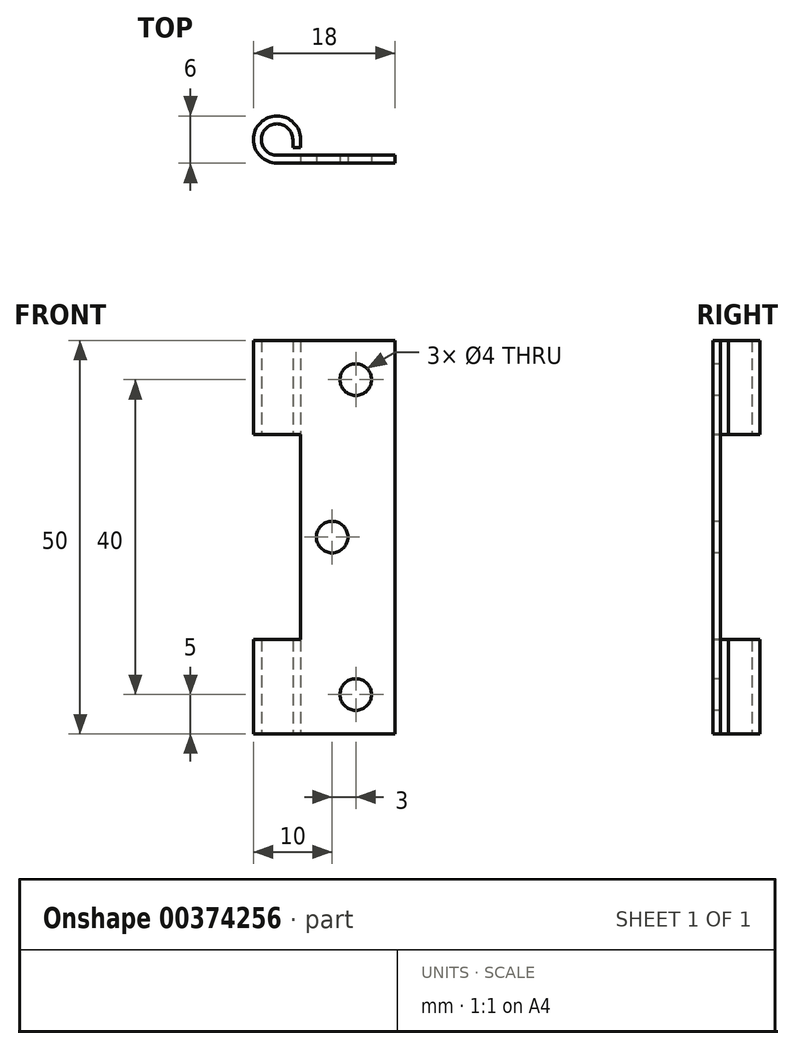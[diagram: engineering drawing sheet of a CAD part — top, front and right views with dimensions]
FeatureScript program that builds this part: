
annotation { "Feature Type Name" : "Feature", "Feature Type Description" : "" }
export const myFeature = defineFeature(function(context is Context, id is Id, definition is map)
    precondition{}
    {
        {
            var Q0;
            Q0=qCreatedBy(makeId("Top.planeOp"),FACE);
            var sketch = newSketch(context, id + "F0", { "sketchPlane" : qUnion([Q0])});
            skLineSegment(sketch, "E0", {"start": v(15, 0) * mm, "end": v(0, 0) * mm});
            skArc(sketch, "E1", {"start": v(3, 3) * mm, "mid": v(-2.12, 5.12) * mm, "end": v(0, 0) * mm});
            skArc(sketch, "E2", {"start": v(2, 3) * mm, "mid": v(-1.41, 4.41) * mm, "end": v(0, 1) * mm});
            skLineSegment(sketch, "E3", {"start": v(0, 1) * mm, "end": v(15, 1) * mm});
            skLineSegment(sketch, "E4", {"start": v(15, 1) * mm, "end": v(15, 0) * mm});
            skLineSegment(sketch, "E5", {"start": v(2, 3) * mm, "end": v(2, 2) * mm});
            skLineSegment(sketch, "E6", {"start": v(2, 2) * mm, "end": v(3, 2) * mm});
            skLineSegment(sketch, "E7", {"start": v(3, 2) * mm, "end": v(3, 3) * mm});
            skSolve(sketch);
        }
        {
            var Q0;
            Q0=makeQuery(id+"F0.imprint","IMPRINT",FACE,{"disambiguationData":[TD([[makeQuery(id+"F0.imprint","IMPRINT",EDGE,{"derivedFrom":sQuery(id+"F0.wireOp",EDGE,"E0")}),-1.0]])]});
            extrude(context, id + "F1", {"entities" : qUnion([Q0]), "depth" : 50 * mm});
        }
        {
            var Q0;
            Q0=qCreatedBy(makeId("Front.planeOp"),FACE);
            var sketch = newSketch(context, id + "F2", { "sketchPlane" : qUnion([Q0])});
            skPoint(sketch, "E8", {"position": v(10, 45) * mm});
            skPoint(sketch, "E9", {"position": v(10, 5) * mm});
            skPoint(sketch, "E10", {"position": v(7, 25) * mm});
            skLineSegment(sketch, "E11.bottom", {"start": v(-5, 38) * mm, "end": v(3, 38) * mm});
            skLineSegment(sketch, "E11.top", {"start": v(-5, 12) * mm, "end": v(3, 12) * mm});
            skLineSegment(sketch, "E11.left", {"start": v(-5, 38) * mm, "end": v(-5, 12) * mm});
            skLineSegment(sketch, "E11.right", {"start": v(3, 38) * mm, "end": v(3, 12) * mm});
            skSolve(sketch);
        }
        {
            var Q0;
            Q0=sQuery(id+"F2.wireOp",VERTEX,"E8");
            var Q1;
            Q1=sQuery(id+"F2.wireOp",VERTEX,"E10");
            var Q2;
            Q2=sQuery(id+"F2.wireOp",VERTEX,"E9");
            var Q3;
            Q3=makeQuery(id+"F1.opExtrude","SWEPT_BODY",BODY,{"disambiguationData":[OSD([sQuery(id+"F0.wireOp",EDGE,"E0"),sQuery(id+"F0.wireOp",EDGE,"E1"),sQuery(id+"F0.wireOp",EDGE,"E2"),sQuery(id+"F0.wireOp",EDGE,"E3"),sQuery(id+"F0.wireOp",EDGE,"E4"),sQuery(id+"F0.wireOp",EDGE,"E5"),sQuery(id+"F0.wireOp",EDGE,"E6"),sQuery(id+"F0.wireOp",EDGE,"E7")])]});
            hole(context, id + "F3", {"style" : HoleStyle.SIMPLE, "endStyle" : HoleEndStyle.BLIND, "holeDiameter" : 4 * mm, "holeDepth" : 10 * mm, "isTappedThrough" : true, "tappedDepth" : 12 * mm, "tapClearance" : 3, "locations" : qUnion([Q0, Q1, Q2]), "scope" : qUnion([Q3])});
        }
        {
            var Q0;
            Q0=makeQuery(id+"F2.imprint","IMPRINT",FACE,{"disambiguationData":[TD([[makeQuery(id+"F2.imprint","IMPRINT",EDGE,{"derivedFrom":sQuery(id+"F2.wireOp",EDGE,"E11.bottom")}),-1.0]])]});
            extrude(context, id + "F4", {"entities" : qUnion([Q0]), "operationType" : NewBodyOperationType.REMOVE, "oppositeDirection" : true, "depth" : 25 * mm});
        }
    });
